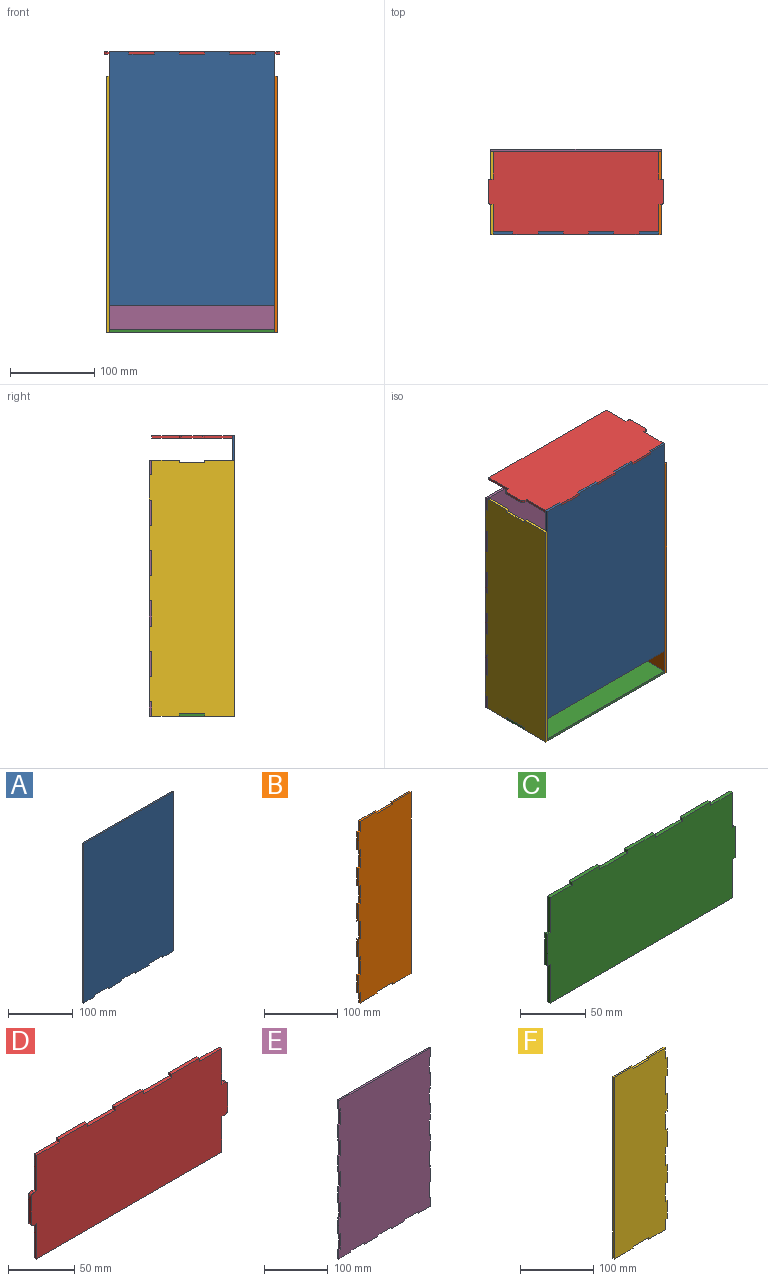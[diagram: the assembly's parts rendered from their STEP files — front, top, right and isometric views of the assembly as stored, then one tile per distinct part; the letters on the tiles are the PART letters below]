
ASSEMBLY  parts=6 mates=5
PART A: 18 faces, bbox 197.2x3x301.8 mm
  f0: plane 301.8x3mm, normal (-1,0,0), area 904.6mm2, adj f1,f15,f16,f17
  f1: plane 23.67x3mm, normal (0,0,-1), area 71mm2, adj f0,f2,f16,f17
  f2: plane 3x3mm, normal (1,0,0), area 9mm2, adj f1,f3,f16,f17
  f3: plane 29.97x3mm, normal (0,0,-1), area 89.8mm2, adj f2,f4,f16,f17
  f4: plane 3x3mm, normal (-1,0,0), area 9mm2, adj f3,f5,f16,f17
  f5: plane 29.97x3mm, normal (0,0,-1), area 89.8mm2, adj f4,f6,f16,f17
  f6: plane 3x3mm, normal (1,0,0), area 9mm2, adj f5,f7,f16,f17
  f7: plane 29.97x3mm, normal (0,0,-1), area 89.8mm2, adj f6,f8,f16,f17
  f8: plane 3x3mm, normal (-1,0,0), area 9mm2, adj f7,f9,f16,f17
  f9: plane 29.97x3mm, normal (0,0,-1), area 89.8mm2, adj f8,f10,f16,f17
  f10: plane 3x3mm, normal (1,0,0), area 9mm2, adj f9,f11,f16,f17
  f11: plane 29.97x3mm, normal (0,0,-1), area 89.8mm2, adj f10,f12,f16,f17
  f12: plane 3x3mm, normal (-1,0,0), area 9mm2, adj f11,f13,f16,f17
  f13: plane 23.67x3mm, normal (0,0,-1), area 71mm2, adj f12,f14,f16,f17
  f14: plane 301.8x3mm, normal (1,0,0), area 904.6mm2, adj f13,f15,f16,f17
  f15: plane 197.21x3mm, normal (0,0,1), area 591.1mm2, adj f0,f14,f16,f17
  f16: plane 301.8x197.21mm, normal (0,-1,0), area 59247.7mm2, adj f0,f1,f2,f3,f4,f5,f6,f7
  f17: plane 301.8x197.21mm, normal (0,1,0), area 59247.7mm2, adj f0,f1,f2,f3,f4,f5,f6,f7
PART B: 34 faces, bbox 101.6x3x304.8 mm
  f0: plane 3x3mm, normal (1,0,0), area 9mm2, adj f1,f31,f32,f33
  f1: plane 32.82x3mm, normal (0,0,1), area 98.4mm2, adj f0,f2,f32,f33
  f2: plane 17.53x3mm, normal (-1,0,0), area 52.5mm2, adj f1,f3,f32,f33
  f3: plane 3x3mm, normal (0,0,1), area 9mm2, adj f2,f4,f32,f33
  f4: plane 29.97x3mm, normal (-1,0,0), area 89.8mm2, adj f3,f5,f32,f33
  f5: plane 3x3mm, normal (0,0,-1), area 9mm2, adj f4,f6,f32,f33
  f6: plane 29.97x3mm, normal (-1,0,0), area 89.8mm2, adj f5,f7,f32,f33
  f7: plane 3x3mm, normal (0,0,1), area 9mm2, adj f6,f8,f32,f33
  f8: plane 29.97x3mm, normal (-1,0,0), area 89.8mm2, adj f7,f9,f32,f33
  f9: plane 3x3mm, normal (0,0,-1), area 9mm2, adj f8,f10,f32,f33
  f10: plane 29.97x3mm, normal (-1,0,0), area 89.8mm2, adj f9,f11,f32,f33
  f11: plane 3x3mm, normal (0,0,1), area 9mm2, adj f10,f12,f32,f33
  f12: plane 29.97x3mm, normal (-1,0,0), area 89.8mm2, adj f11,f13,f32,f33
  f13: plane 3x3mm, normal (0,0,-1), area 9mm2, adj f12,f14,f32,f33
  f14: plane 29.97x3mm, normal (-1,0,0), area 89.8mm2, adj f13,f15,f32,f33
  f15: plane 3x3mm, normal (0,0,1), area 9mm2, adj f14,f16,f32,f33
  f16: plane 29.97x3mm, normal (-1,0,0), area 89.8mm2, adj f15,f17,f32,f33
  f17: plane 3x3mm, normal (0,0,-1), area 9mm2, adj f16,f18,f32,f33
  f18: plane 29.97x3mm, normal (-1,0,0), area 89.8mm2, adj f17,f19,f32,f33
  f19: plane 3x3mm, normal (0,0,1), area 9mm2, adj f18,f20,f32,f33
  f20: plane 29.97x3mm, normal (-1,0,0), area 89.8mm2, adj f19,f21,f32,f33
  f21: plane 3x3mm, normal (0,0,-1), area 9mm2, adj f20,f22,f32,f33
  f22: plane 17.53x3mm, normal (-1,0,0), area 52.5mm2, adj f21,f23,f32,f33
  f23: plane 32.82x3mm, normal (0,0,-1), area 98.4mm2, adj f22,f24,f32,f33
  f24: plane 3x3mm, normal (1,0,0), area 9mm2, adj f23,f25,f32,f33
  f25: plane 29.97x3mm, normal (0,0,-1), area 89.8mm2, adj f24,f26,f32,f33
  f26: plane 3x3mm, normal (-1,0,0), area 9mm2, adj f25,f27,f32,f33
  f27: plane 35.81x3mm, normal (0,0,-1), area 107.3mm2, adj f26,f28,f32,f33
  f28: plane 304.8x3mm, normal (1,0,0), area 913.5mm2, adj f27,f29,f32,f33
  f29: plane 35.81x3mm, normal (0,0,1), area 107.3mm2, adj f28,f30,f32,f33
  f30: plane 3x3mm, normal (-1,0,0), area 9mm2, adj f29,f31,f32,f33
  f31: plane 29.97x3mm, normal (0,0,1), area 89.8mm2, adj f0,f30,f32,f33
  f32: plane 304.8x101.6mm, normal (0,-1,0), area 30323.6mm2, adj f0,f1,f2,f3,f4,f5,f6,f7
  f33: plane 304.8x101.6mm, normal (0,1,0), area 30323.6mm2, adj f0,f1,f2,f3,f4,f5,f6,f7
PART C: 26 faces, bbox 203.2x3x101.6 mm
  f0: plane 197.21x3mm, normal (0,0,-1), area 591.1mm2, adj f1,f23,f24,f25
  f1: plane 35.81x3mm, normal (1,0,0), area 107.3mm2, adj f0,f2,f24,f25
  f2: plane 3x3mm, normal (0,0,-1), area 9mm2, adj f1,f3,f24,f25
  f3: plane 29.97x3mm, normal (1,0,0), area 89.8mm2, adj f2,f4,f24,f25
  f4: plane 3x3mm, normal (0,0,1), area 9mm2, adj f3,f5,f24,f25
  f5: plane 32.82x3mm, normal (1,0,0), area 98.4mm2, adj f4,f6,f24,f25
  f6: plane 23.67x3mm, normal (0,0,1), area 71mm2, adj f5,f7,f24,f25
  f7: plane 3x3mm, normal (1,0,0), area 9mm2, adj f6,f8,f24,f25
  f8: plane 29.97x3mm, normal (0,0,1), area 89.8mm2, adj f7,f9,f24,f25
  f9: plane 3x3mm, normal (-1,0,0), area 9mm2, adj f8,f10,f24,f25
  f10: plane 29.97x3mm, normal (0,0,1), area 89.8mm2, adj f9,f11,f24,f25
  f11: plane 3x3mm, normal (1,0,0), area 9mm2, adj f10,f12,f24,f25
  f12: plane 29.97x3mm, normal (0,0,1), area 89.8mm2, adj f11,f13,f24,f25
  f13: plane 3x3mm, normal (-1,0,0), area 9mm2, adj f12,f14,f24,f25
  f14: plane 29.97x3mm, normal (0,0,1), area 89.8mm2, adj f13,f15,f24,f25
  f15: plane 3x3mm, normal (1,0,0), area 9mm2, adj f14,f16,f24,f25
  f16: plane 29.97x3mm, normal (0,0,1), area 89.8mm2, adj f15,f17,f24,f25
  f17: plane 3x3mm, normal (-1,0,0), area 9mm2, adj f16,f18,f24,f25
  f18: plane 23.67x3mm, normal (0,0,1), area 71mm2, adj f17,f19,f24,f25
  f19: plane 32.82x3mm, normal (-1,0,0), area 98.4mm2, adj f18,f20,f24,f25
  f20: plane 3x3mm, normal (0,0,1), area 9mm2, adj f19,f21,f24,f25
  f21: plane 29.97x3mm, normal (-1,0,0), area 89.8mm2, adj f20,f22,f24,f25
  f22: plane 3x3mm, normal (0,0,-1), area 9mm2, adj f21,f23,f24,f25
  f23: plane 35.81x3mm, normal (-1,0,0), area 107.3mm2, adj f0,f22,f24,f25
  f24: plane 203.2x101.6mm, normal (0,-1,0), area 19894.2mm2, adj f0,f1,f2,f3,f4,f5,f6,f7
  f25: plane 203.2x101.6mm, normal (0,1,0), area 19894.2mm2, adj f0,f1,f2,f3,f4,f5,f6,f7
PART D: 30 faces, bbox 209.2x3x98.6 mm
  f0: plane 23.67x3mm, normal (0,0,1), area 71mm2, adj f1,f27,f28,f29
  f1: plane 3x3mm, normal (1,0,0), area 9mm2, adj f0,f2,f28,f29
  f2: plane 29.97x3mm, normal (0,0,1), area 89.8mm2, adj f1,f3,f28,f29
  f3: plane 3x3mm, normal (-1,0,0), area 9mm2, adj f2,f4,f28,f29
  f4: plane 29.97x3mm, normal (0,0,1), area 89.8mm2, adj f3,f5,f28,f29
  f5: plane 3x3mm, normal (1,0,0), area 9mm2, adj f4,f6,f28,f29
  f6: plane 29.97x3mm, normal (0,0,1), area 89.8mm2, adj f5,f7,f28,f29
  f7: plane 3x3mm, normal (-1,0,0), area 9mm2, adj f6,f8,f28,f29
  f8: plane 29.97x3mm, normal (0,0,1), area 89.8mm2, adj f7,f9,f28,f29
  f9: plane 3x3mm, normal (1,0,0), area 9mm2, adj f8,f10,f28,f29
  f10: plane 29.97x3mm, normal (0,0,1), area 89.8mm2, adj f9,f11,f28,f29
  f11: plane 3x3mm, normal (-1,0,0), area 9mm2, adj f10,f12,f28,f29
  f12: plane 23.67x3mm, normal (0,0,1), area 71mm2, adj f11,f13,f28,f29
  f13: plane 32.82x3mm, normal (-1,0,0), area 98.4mm2, adj f12,f14,f28,f29
  f14: plane 3x3mm, normal (0,0,1), area 9mm2, adj f13,f15,f28,f29
  f15: cylinder r=3mm len=3mm, axis (0,1,0), area 14.1mm2, adj f14,f16,f28,f29
  f16: plane 23.98x3mm, normal (-1,0,0), area 71.9mm2, adj f15,f17,f28,f29
  f17: cylinder r=3mm len=3mm, axis (0,1,0), area 14.1mm2, adj f16,f18,f28,f29
  f18: plane 3x3mm, normal (0,0,-1), area 9mm2, adj f17,f19,f28,f29
  f19: plane 32.82x3mm, normal (-1,0,0), area 98.4mm2, adj f18,f20,f28,f29
  f20: plane 197.21x3mm, normal (0,0,-1), area 591.1mm2, adj f19,f21,f28,f29
  f21: plane 32.82x3mm, normal (1,0,0), area 98.4mm2, adj f20,f22,f28,f29
  f22: plane 3x3mm, normal (0,0,-1), area 9mm2, adj f21,f23,f28,f29
  f23: cylinder r=3mm len=3mm, axis (0,1,0), area 14.1mm2, adj f22,f24,f28,f29
  f24: plane 23.98x3mm, normal (1,0,0), area 71.9mm2, adj f23,f25,f28,f29
  f25: cylinder r=3mm len=3mm, axis (0,1,0), area 14.1mm2, adj f24,f26,f28,f29
  f26: plane 3x3mm, normal (0,0,1), area 9mm2, adj f25,f27,f28,f29
  f27: plane 32.82x3mm, normal (1,0,0), area 98.4mm2, adj f0,f26,f28,f29
  f28: plane 209.19x98.6mm, normal (0,-1,0), area 19475.1mm2, adj f0,f1,f2,f3,f4,f5,f6,f7
  f29: plane 209.19x98.6mm, normal (0,1,0), area 19475.1mm2, adj f0,f1,f2,f3,f4,f5,f6,f7
PART E: 58 faces, bbox 203.2x3x304.8 mm
  f0: plane 203.2x3mm, normal (0,0,1), area 609mm2, adj f1,f55,f56,f57
  f1: plane 17.53x3mm, normal (-1,0,0), area 52.5mm2, adj f0,f2,f56,f57
  f2: plane 3x3mm, normal (0,0,-1), area 9mm2, adj f1,f3,f56,f57
  f3: plane 29.97x3mm, normal (-1,0,0), area 89.8mm2, adj f2,f4,f56,f57
  f4: plane 3x3mm, normal (0,0,1), area 9mm2, adj f3,f5,f56,f57
  f5: plane 29.97x3mm, normal (-1,0,0), area 89.8mm2, adj f4,f6,f56,f57
  f6: plane 3x3mm, normal (0,0,-1), area 9mm2, adj f5,f7,f56,f57
  f7: plane 29.97x3mm, normal (-1,0,0), area 89.8mm2, adj f6,f8,f56,f57
  f8: plane 3x3mm, normal (0,0,1), area 9mm2, adj f7,f9,f56,f57
  f9: plane 29.97x3mm, normal (-1,0,0), area 89.8mm2, adj f8,f10,f56,f57
  f10: plane 3x3mm, normal (0,0,-1), area 9mm2, adj f9,f11,f56,f57
  f11: plane 29.97x3mm, normal (-1,0,0), area 89.8mm2, adj f10,f12,f56,f57
  f12: plane 3x3mm, normal (0,0,1), area 9mm2, adj f11,f13,f56,f57
  f13: plane 29.97x3mm, normal (-1,0,0), area 89.8mm2, adj f12,f14,f56,f57
  f14: plane 3x3mm, normal (0,0,-1), area 9mm2, adj f13,f15,f56,f57
  f15: plane 29.97x3mm, normal (-1,0,0), area 89.8mm2, adj f14,f16,f56,f57
  f16: plane 3x3mm, normal (0,0,1), area 9mm2, adj f15,f17,f56,f57
  f17: plane 29.97x3mm, normal (-1,0,0), area 89.8mm2, adj f16,f18,f56,f57
  f18: plane 3x3mm, normal (0,0,-1), area 9mm2, adj f17,f19,f56,f57
  f19: plane 29.97x3mm, normal (-1,0,0), area 89.8mm2, adj f18,f20,f56,f57
  f20: plane 3x3mm, normal (0,0,1), area 9mm2, adj f19,f21,f56,f57
  f21: plane 17.53x3mm, normal (-1,0,0), area 52.5mm2, adj f20,f22,f56,f57
  f22: plane 26.67x3mm, normal (0,0,-1), area 79.9mm2, adj f21,f23,f56,f57
  f23: plane 3x3mm, normal (1,0,0), area 9mm2, adj f22,f24,f56,f57
  f24: plane 29.97x3mm, normal (0,0,-1), area 89.8mm2, adj f23,f25,f56,f57
  f25: plane 3x3mm, normal (-1,0,0), area 9mm2, adj f24,f26,f56,f57
  f26: plane 29.97x3mm, normal (0,0,-1), area 89.8mm2, adj f25,f27,f56,f57
  f27: plane 3x3mm, normal (1,0,0), area 9mm2, adj f26,f28,f56,f57
  f28: plane 29.97x3mm, normal (0,0,-1), area 89.8mm2, adj f27,f29,f56,f57
  f29: plane 3x3mm, normal (-1,0,0), area 9mm2, adj f28,f30,f56,f57
  f30: plane 29.97x3mm, normal (0,0,-1), area 89.8mm2, adj f29,f31,f56,f57
  f31: plane 3x3mm, normal (1,0,0), area 9mm2, adj f30,f32,f56,f57
  f32: plane 29.97x3mm, normal (0,0,-1), area 89.8mm2, adj f31,f33,f56,f57
  f33: plane 3x3mm, normal (-1,0,0), area 9mm2, adj f32,f34,f56,f57
  f34: plane 26.67x3mm, normal (0,0,-1), area 79.9mm2, adj f33,f35,f56,f57
  f35: plane 17.53x3mm, normal (1,0,0), area 52.5mm2, adj f34,f36,f56,f57
  f36: plane 3x3mm, normal (0,0,1), area 9mm2, adj f35,f37,f56,f57
  f37: plane 29.97x3mm, normal (1,0,0), area 89.8mm2, adj f36,f38,f56,f57
  f38: plane 3x3mm, normal (0,0,-1), area 9mm2, adj f37,f39,f56,f57
  f39: plane 29.97x3mm, normal (1,0,0), area 89.8mm2, adj f38,f40,f56,f57
  f40: plane 3x3mm, normal (0,0,1), area 9mm2, adj f39,f41,f56,f57
  f41: plane 29.97x3mm, normal (1,0,0), area 89.8mm2, adj f40,f42,f56,f57
  f42: plane 3x3mm, normal (0,0,-1), area 9mm2, adj f41,f43,f56,f57
  f43: plane 29.97x3mm, normal (1,0,0), area 89.8mm2, adj f42,f44,f56,f57
  f44: plane 3x3mm, normal (0,0,1), area 9mm2, adj f43,f45,f56,f57
  f45: plane 29.97x3mm, normal (1,0,0), area 89.8mm2, adj f44,f46,f56,f57
  f46: plane 3x3mm, normal (0,0,-1), area 9mm2, adj f45,f47,f56,f57
  f47: plane 29.97x3mm, normal (1,0,0), area 89.8mm2, adj f46,f48,f56,f57
  f48: plane 3x3mm, normal (0,0,1), area 9mm2, adj f47,f49,f56,f57
  f49: plane 29.97x3mm, normal (1,0,0), area 89.8mm2, adj f48,f50,f56,f57
  f50: plane 3x3mm, normal (0,0,-1), area 9mm2, adj f49,f51,f56,f57
  f51: plane 29.97x3mm, normal (1,0,0), area 89.8mm2, adj f50,f52,f56,f57
  f52: plane 3x3mm, normal (0,0,1), area 9mm2, adj f51,f53,f56,f57
  f53: plane 29.97x3mm, normal (1,0,0), area 89.8mm2, adj f52,f54,f56,f57
  f54: plane 3x3mm, normal (0,0,-1), area 9mm2, adj f53,f55,f56,f57
  f55: plane 17.53x3mm, normal (1,0,0), area 52.5mm2, adj f0,f54,f56,f57
  f56: plane 304.8x203.2mm, normal (0,-1,0), area 60767.5mm2, adj f0,f1,f2,f3,f4,f5,f6,f7
  f57: plane 304.8x203.2mm, normal (0,1,0), area 60767.5mm2, adj f0,f1,f2,f3,f4,f5,f6,f7
PART F: 34 faces, bbox 101.6x3x304.8 mm
  f0: plane 3x3mm, normal (-1,0,0), area 9mm2, adj f1,f31,f32,f33
  f1: plane 32.82x3mm, normal (0,0,-1), area 98.4mm2, adj f0,f2,f32,f33
  f2: plane 17.53x3mm, normal (1,0,0), area 52.5mm2, adj f1,f3,f32,f33
  f3: plane 3x3mm, normal (0,0,-1), area 9mm2, adj f2,f4,f32,f33
  f4: plane 29.97x3mm, normal (1,0,0), area 89.8mm2, adj f3,f5,f32,f33
  f5: plane 3x3mm, normal (0,0,1), area 9mm2, adj f4,f6,f32,f33
  f6: plane 29.97x3mm, normal (1,0,0), area 89.8mm2, adj f5,f7,f32,f33
  f7: plane 3x3mm, normal (0,0,-1), area 9mm2, adj f6,f8,f32,f33
  f8: plane 29.97x3mm, normal (1,0,0), area 89.8mm2, adj f7,f9,f32,f33
  f9: plane 3x3mm, normal (0,0,1), area 9mm2, adj f8,f10,f32,f33
  f10: plane 29.97x3mm, normal (1,0,0), area 89.8mm2, adj f9,f11,f32,f33
  f11: plane 3x3mm, normal (0,0,-1), area 9mm2, adj f10,f12,f32,f33
  f12: plane 29.97x3mm, normal (1,0,0), area 89.8mm2, adj f11,f13,f32,f33
  f13: plane 3x3mm, normal (0,0,1), area 9mm2, adj f12,f14,f32,f33
  f14: plane 29.97x3mm, normal (1,0,0), area 89.8mm2, adj f13,f15,f32,f33
  f15: plane 3x3mm, normal (0,0,-1), area 9mm2, adj f14,f16,f32,f33
  f16: plane 29.97x3mm, normal (1,0,0), area 89.8mm2, adj f15,f17,f32,f33
  f17: plane 3x3mm, normal (0,0,1), area 9mm2, adj f16,f18,f32,f33
  f18: plane 29.97x3mm, normal (1,0,0), area 89.8mm2, adj f17,f19,f32,f33
  f19: plane 3x3mm, normal (0,0,-1), area 9mm2, adj f18,f20,f32,f33
  f20: plane 29.97x3mm, normal (1,0,0), area 89.8mm2, adj f19,f21,f32,f33
  f21: plane 3x3mm, normal (0,0,1), area 9mm2, adj f20,f22,f32,f33
  f22: plane 17.53x3mm, normal (1,0,0), area 52.5mm2, adj f21,f23,f32,f33
  f23: plane 32.82x3mm, normal (0,0,1), area 98.4mm2, adj f22,f24,f32,f33
  f24: plane 3x3mm, normal (-1,0,0), area 9mm2, adj f23,f25,f32,f33
  f25: plane 29.97x3mm, normal (0,0,1), area 89.8mm2, adj f24,f26,f32,f33
  f26: plane 3x3mm, normal (1,0,0), area 9mm2, adj f25,f27,f32,f33
  f27: plane 35.81x3mm, normal (0,0,1), area 107.3mm2, adj f26,f28,f32,f33
  f28: plane 304.8x3mm, normal (-1,0,0), area 913.5mm2, adj f27,f29,f32,f33
  f29: plane 35.81x3mm, normal (0,0,-1), area 107.3mm2, adj f28,f30,f32,f33
  f30: plane 3x3mm, normal (1,0,0), area 9mm2, adj f29,f31,f32,f33
  f31: plane 29.97x3mm, normal (0,0,-1), area 89.8mm2, adj f0,f30,f32,f33
  f32: plane 304.8x101.6mm, normal (0,-1,0), area 30323.6mm2, adj f0,f1,f2,f3,f4,f5,f6,f7
  f33: plane 304.8x101.6mm, normal (0,1,0), area 30323.6mm2, adj f0,f1,f2,f3,f4,f5,f6,f7
PLACE A rot(axis=(-1,0,0),180deg) t=(-57.69,-17.92,117.71)mm
PLACE B rot(axis=(0,0,-1),90deg) t=(81.69,245.46,1.06)mm
PLACE C rot(axis=(-1,0,0),90deg) t=(-54.69,438.96,-334.07)mm
PLACE D rot(axis=(1,0,0),90deg) t=(-54.69,70.67,-0.12)mm
PLACE E t=(-54.69,83.68,1.06)mm
PLACE F rot(axis=(0,0,1),90deg) t=(-121.51,176.36,1.06)mm
MATE fastened F.f21 <-> E.f2  axis (0,0,1) through (-120.01,82.18,-46.8)mm
MATE fastened E.f54 <-> B.f3  axis (0,0,-1) through (80.19,82.18,-46.8)mm
MATE fastened E.f33 <-> C.f7  axis (-1,0,0) through (55.02,82.18,-332.57)mm
MATE fastened D.f1 <-> A.f12  axis (1,0,0) through (55.02,-16.42,-1.62)mm
MATE slider D.f28 <-> B.f1  axis (0,0,-1) through (78.69,64.28,-3.12)mm
